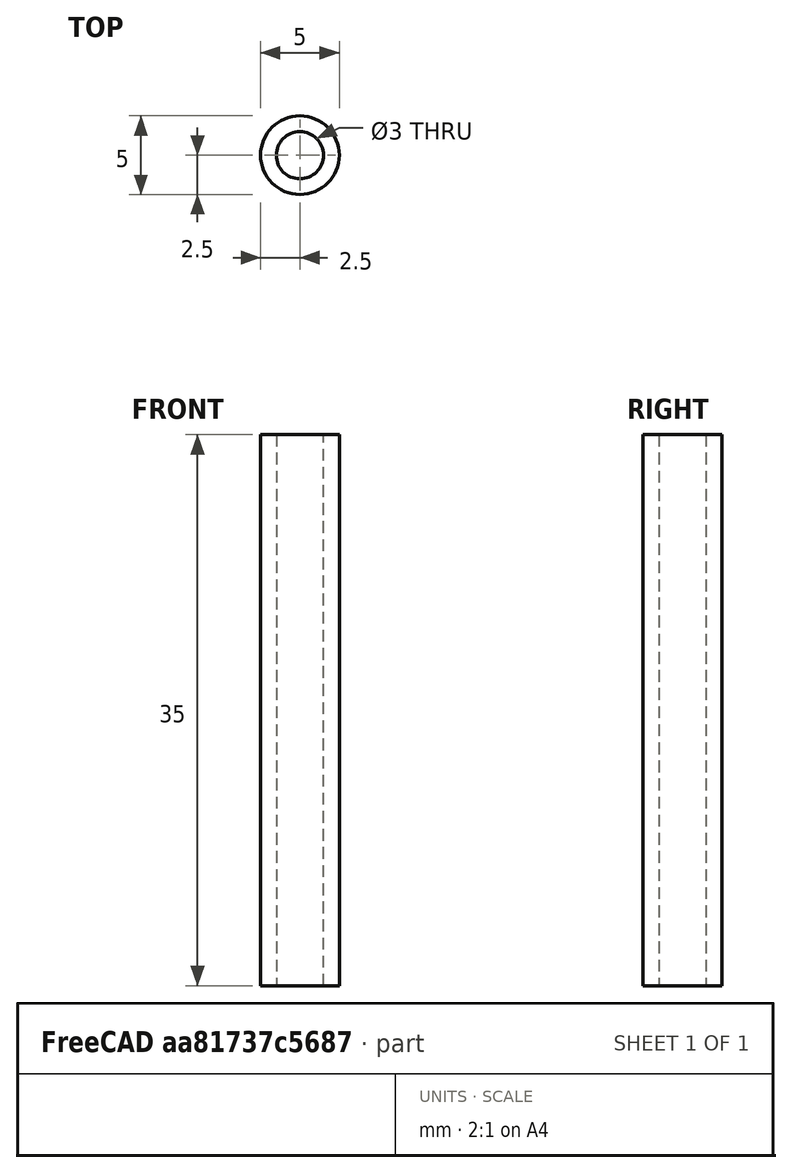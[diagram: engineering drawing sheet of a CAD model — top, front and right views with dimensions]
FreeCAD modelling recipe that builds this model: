
FCSTD DOCUMENT  (FreeCAD 0.20R29410 (Git))
Label: back_pillar
License: All rights reserved
LicenseURL: http://en.wikipedia.org/wiki/All_rights_reserved
objects: PartDesign::CoordinateSystem×2, Sketcher::SketchObject×1, PartDesign::Pad×1, PartDesign::Body×1
note: 6 computed .brp shape members not serialized (recipe doc carries the construction recipe); baked Part::Feature solids carry a one-line shape summary decoded from their .brp

FEATURE [Sketcher::SketchObject] Sketch
  FullyConstrained = true
  MapMode = 5
  Support = -> [XY_Plane]
  sketch-geometry (2):
    g0: Circle CenterX=0 CenterY=0 CenterZ=0 NormalX=0 NormalY=0 NormalZ=1 AngleXU=0 Radius=2.5
    g1: Circle CenterX=0 CenterY=0 CenterZ=0 NormalX=0 NormalY=0 NormalZ=1 AngleXU=0 Radius=1.5
  constraints (4):
    c: Coincident(g0,g-1)
    c: Coincident(g1,g0)
    c: Diameter(g0) = 5
    c: Diameter(g1) = 3
FEATURE [PartDesign::Pad] Pad
  Direction = (0,0,1)
  Length = 35
  Length2 = 10
  Profile = -> Sketch
  ReferenceAxis = -> Sketch [N_Axis]
  Type = 0
FEATURE [PartDesign::CoordinateSystem] LCS_1
  AttacherType = Attacher::AttachEngine3D
  MapMode = 11
  Placement = pos=(0,0,0) rot=(0,0,1;1.5708rad)
  Support = -> [Pad]
FEATURE [PartDesign::CoordinateSystem] LCS_2
  AttacherType = Attacher::AttachEngine3D
  MapMode = 11
  Placement = pos=(0,0,35) rot=(0,0,1;1.5708rad)
  Support = -> [Pad]
FEATURE [PartDesign::Body] Body
  Group = -> [Sketch,Pad,LCS_1,LCS_2]
  Origin = -> Origin
  Tip = -> Pad
